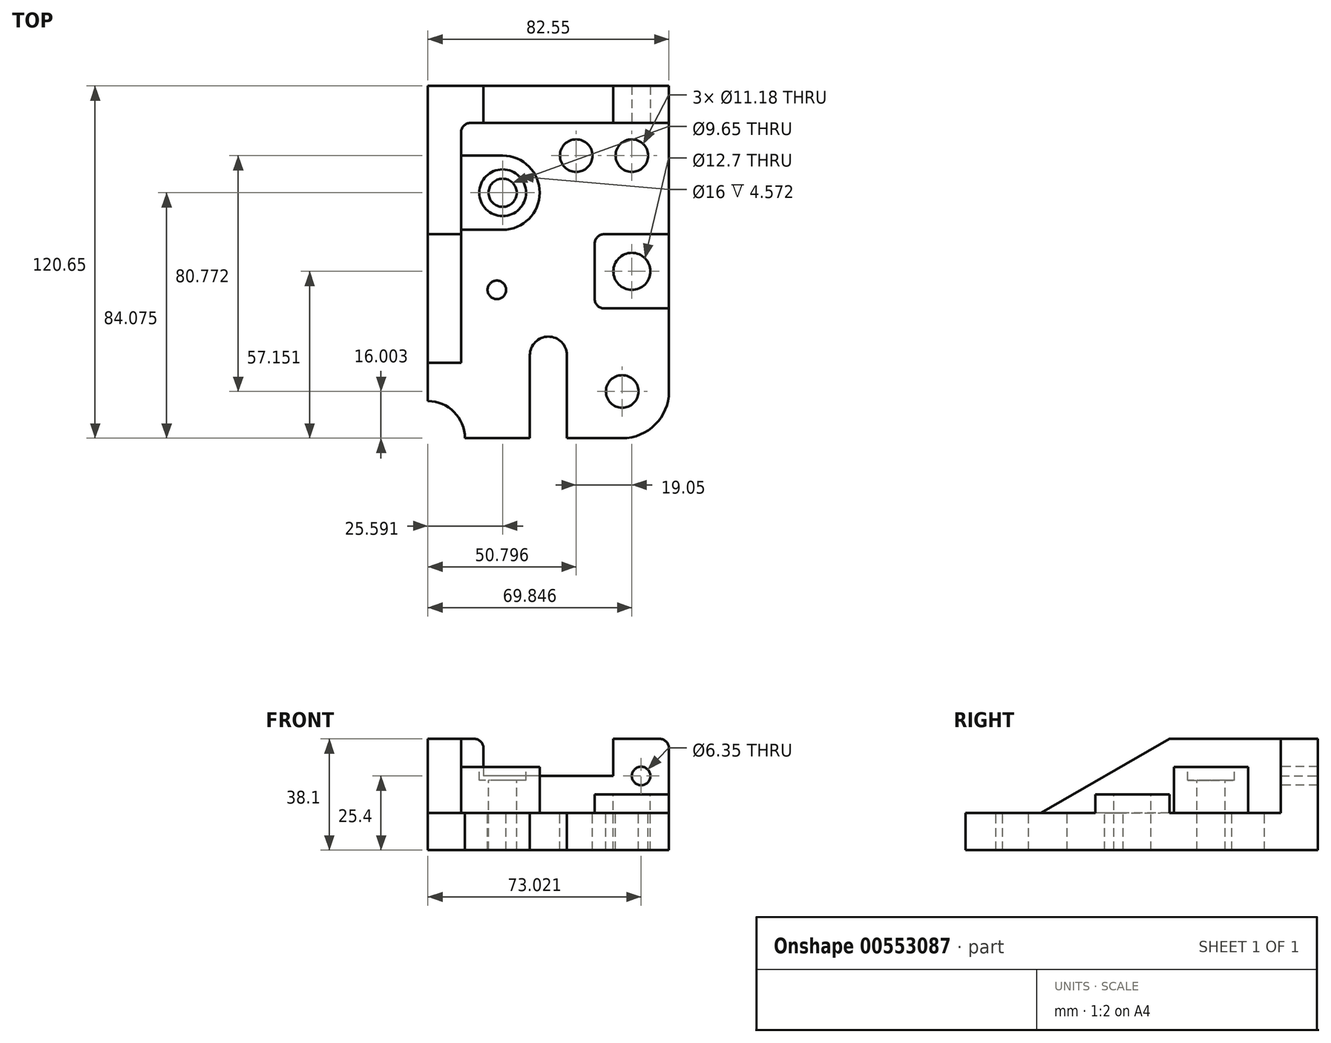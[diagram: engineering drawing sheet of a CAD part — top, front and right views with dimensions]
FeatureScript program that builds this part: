
annotation { "Feature Type Name" : "Feature", "Feature Type Description" : "" }
export const myFeature = defineFeature(function(context is Context, id is Id, definition is map)
    precondition{}
    {
        {
            var Q0;
            Q0=qCreatedBy(makeId("Top.planeOp"),FACE);
            var sketch = newSketch(context, id + "F0", { "sketchPlane" : qUnion([Q0])});
            skLineSegment(sketch, "E0.bottom", {"start": v(-42.14, 89.34) * mm, "end": v(40.4, 89.34) * mm});
            skLineSegment(sketch, "E0.top", {"start": v(-42.14, -31.3) * mm, "end": v(40.4, -31.3) * mm});
            skLineSegment(sketch, "E0.left", {"start": v(-42.14, 89.34) * mm, "end": v(-42.14, -31.3) * mm});
            skLineSegment(sketch, "E0.right", {"start": v(40.4, 89.34) * mm, "end": v(40.4, -31.3) * mm});
            skSolve(sketch);
        }
        {
            var Q0;
            Q0=makeQuery(id+"F0.imprint","IMPRINT",FACE,{"disambiguationData":[TD([[makeQuery(id+"F0.imprint","IMPRINT",EDGE,{"derivedFrom":sQuery(id+"F0.wireOp",EDGE,"E0.bottom")}),-1.0]])]});
            extrude(context, id + "F1", {"entities" : qUnion([Q0]), "depth" : 12.7 * mm, "offsetDistance" : 25.4 * mm});
        }
        {
            var Q0;
            Q0=makeQuery(id+"F1.opExtrude","CAP_FACE",FACE,{"disambiguationData":[OSD([sQuery(id+"F0.wireOp",EDGE,"E0.bottom"),sQuery(id+"F0.wireOp",EDGE,"E0.top"),sQuery(id+"F0.wireOp",EDGE,"E0.left"),sQuery(id+"F0.wireOp",EDGE,"E0.right")])],"isStart":false});
            var sketch = newSketch(context, id + "F2", { "sketchPlane" : qUnion([Q0])});
            skLineSegment(sketch, "E1.bottom", {"start": v(-42.14, 89.34) * mm, "end": v(40.4, 89.34) * mm});
            skLineSegment(sketch, "E1.top", {"start": v(-30.77, 76.64) * mm, "end": v(40.4, 76.64) * mm});
            skLineSegment(sketch, "E1.left", {"start": v(-42.14, 89.34) * mm, "end": v(-42.14, 76.64) * mm});
            skLineSegment(sketch, "E1.right", {"start": v(40.4, 89.34) * mm, "end": v(40.4, 76.64) * mm});
            skLineSegment(sketch, "E2.bottom", {"start": v(-42.14, 89.34) * mm, "end": v(-30.77, 89.34) * mm});
            skLineSegment(sketch, "E2.top", {"start": v(-42.14, 38.54) * mm, "end": v(-30.77, 38.54) * mm});
            skLineSegment(sketch, "E2.left", {"start": v(-42.14, 89.34) * mm, "end": v(-42.14, 38.54) * mm});
            skLineSegment(sketch, "E2.right", {"start": v(-30.77, 76.64) * mm, "end": v(-30.77, 38.54) * mm});
            skSolve(sketch);
        }
        {
            var Q0;
            Q0=makeQuery(id+"F2.imprint","IMPRINT",FACE,{"disambiguationData":[TD([[makeQuery(id+"F2.imprint","IMPRINT",EDGE,{"derivedFrom":sQuery(id+"F2.wireOp",EDGE,"E1.bottom")}),-1.0]])]});
            extrude(context, id + "F3", {"entities" : qUnion([Q0]), "operationType" : NewBodyOperationType.ADD, "depth" : 25.4 * mm, "offsetDistance" : 25.4 * mm});
        }
        {
            var Q0;
            Q0=makeQuery(id+"F3.opExtrude","SWEPT_FACE",FACE,{"disambiguationData":[OSD([sQuery(id+"F2.wireOp",EDGE,"E2.right")])]});
            var sketch = newSketch(context, id + "F4", { "sketchPlane" : qUnion([Q0])});
            skLineSegment(sketch, "E3", {"start": v(38.54, 38.1) * mm, "end": v(-3.5, 38.1) * mm});
            skLineSegment(sketch, "E4", {"start": v(38.54, 38.1) * mm, "end": v(-5.45, 12.7) * mm});
            skLineSegment(sketch, "E5", {"start": v(38.54, 12.7) * mm, "end": v(-5.45, 12.7) * mm});
            skLineSegment(sketch, "E6", {"start": v(38.54, 38.1) * mm, "end": v(38.54, 12.7) * mm});
            skSolve(sketch);
        }
        {
            var Q0;
            Q0=makeQuery(id+"F4.imprint","IMPRINT",FACE,{"disambiguationData":[TD([[makeQuery(id+"F4.imprint","IMPRINT",EDGE,{"derivedFrom":sQuery(id+"F4.wireOp",EDGE,"E4")}),1.0]])]});
            var Q1;
            Q1=makeQuery(id+"F3.boolean.opBoolean","MERGE",FACE,{"derivedFrom":[makeQuery(id+"F1.opExtrude","SWEPT_FACE",FACE,{"disambiguationData":[OSD([sQuery(id+"F0.wireOp",EDGE,"E0.left")])]}),makeQuery(id+"F3.opExtrude","SWEPT_FACE",FACE,{"disambiguationData":[OSD([sQuery(id+"F2.wireOp",EDGE,"E2.left")])]})]});
            extrude(context, id + "F5", {"entities" : qUnion([Q0]), "operationType" : NewBodyOperationType.ADD, "endBound" : BoundingType.UP_TO_SURFACE, "oppositeDirection" : true, "depth" : 18.54 * mm, "endBoundEntityFace" : qUnion([Q1]), "offsetDistance" : 25.4 * mm});
        }
        {
            var Q0;
            Q0=makeQuery(id+"F3.boolean.opBoolean","MERGE",FACE,{"derivedFrom":[makeQuery(id+"F1.opExtrude","SWEPT_FACE",FACE,{"disambiguationData":[OSD([sQuery(id+"F0.wireOp",EDGE,"E0.bottom")])]}),makeQuery(id+"F3.opExtrude","SWEPT_FACE",FACE,{"disambiguationData":[OSD([sQuery(id+"F2.wireOp",EDGE,"E1.bottom"),sQuery(id+"F2.wireOp",EDGE,"E2.bottom")])]})]});
            var sketch = newSketch(context, id + "F6", { "sketchPlane" : qUnion([Q0])});
            skLineSegment(sketch, "E7.bottom", {"start": v(-21.36, 38.1) * mm, "end": v(23.1, 38.1) * mm});
            skLineSegment(sketch, "E7.top", {"start": v(-21.36, 25.4) * mm, "end": v(23.1, 25.4) * mm});
            skLineSegment(sketch, "E7.left", {"start": v(-21.36, 38.1) * mm, "end": v(-21.36, 25.4) * mm});
            skLineSegment(sketch, "E7.right", {"start": v(23.1, 38.1) * mm, "end": v(23.1, 25.4) * mm});
            skSolve(sketch);
        }
        {
            var Q0;
            Q0=makeQuery(id+"F6.imprint","IMPRINT",FACE,{"disambiguationData":[TD([[makeQuery(id+"F6.imprint","IMPRINT",EDGE,{"derivedFrom":sQuery(id+"F6.wireOp",EDGE,"E7.bottom")}),1.0]])]});
            extrude(context, id + "F7", {"entities" : qUnion([Q0]), "operationType" : NewBodyOperationType.REMOVE, "oppositeDirection" : true, "depth" : 25.4 * mm, "offsetDistance" : 25.4 * mm});
        }
        {
            var Q0;
            Q0=makeQuery(id+"F1.opExtrude","CAP_FACE",FACE,{"disambiguationData":[OSD([sQuery(id+"F0.wireOp",EDGE,"E0.bottom"),sQuery(id+"F0.wireOp",EDGE,"E0.top"),sQuery(id+"F0.wireOp",EDGE,"E0.left"),sQuery(id+"F0.wireOp",EDGE,"E0.right")])],"isStart":false});
            var sketch = newSketch(context, id + "F8", { "sketchPlane" : qUnion([Q0])});
            skLineSegment(sketch, "E8.bottom", {"start": v(40.4, 13.14) * mm, "end": v(15, 13.14) * mm});
            skLineSegment(sketch, "E8.top", {"start": v(40.4, 38.54) * mm, "end": v(15, 38.54) * mm});
            skLineSegment(sketch, "E8.left", {"start": v(40.4, 13.14) * mm, "end": v(40.4, 38.54) * mm});
            skLineSegment(sketch, "E8.right", {"start": v(15, 13.14) * mm, "end": v(15, 38.54) * mm});
            skSolve(sketch);
        }
        {
            var Q0;
            Q0=makeQuery(id+"F8.imprint","IMPRINT",FACE,{"disambiguationData":[TD([[makeQuery(id+"F8.imprint","IMPRINT",EDGE,{"derivedFrom":sQuery(id+"F8.wireOp",EDGE,"E8.bottom")}),-1.0]])]});
            extrude(context, id + "F9", {"entities" : qUnion([Q0]), "operationType" : NewBodyOperationType.ADD, "depth" : 6.35 * mm, "offsetDistance" : 25.4 * mm});
        }
        {
            var Q0;
            Q0=makeQuery(id+"F9.opExtrude","CAP_FACE",FACE,{"disambiguationData":[OSD([sQuery(id+"F8.wireOp",EDGE,"E8.bottom"),sQuery(id+"F8.wireOp",EDGE,"E8.top"),sQuery(id+"F8.wireOp",EDGE,"E8.left"),sQuery(id+"F8.wireOp",EDGE,"E8.right")])],"isStart":false});
            var sketch = newSketch(context, id + "F10", { "sketchPlane" : qUnion([Q0])});
            skCircle(sketch, "E9", {"center": v(27.7, 25.84) * mm, "radius": 6.35 * mm});
            skPoint(sketch, "E9.centerSnap0", {"position": v(27.7, 13.14) * mm});
            skPoint(sketch, "E9.centerSnap1", {"position": v(40.4, 25.84) * mm});
            skSolve(sketch);
        }
        {
            var Q0;
            Q0=makeQuery(id+"F10.imprint","IMPRINT",FACE,{"disambiguationData":[TD([[makeQuery(id+"F10.imprint","IMPRINT",EDGE,{"derivedFrom":sQuery(id+"F10.wireOp",EDGE,"E9")}),1.0]])]});
            extrude(context, id + "F11", {"entities" : qUnion([Q0]), "operationType" : NewBodyOperationType.REMOVE, "endBound" : BoundingType.THROUGH_ALL, "oppositeDirection" : true, "depth" : 25.4 * mm, "offsetDistance" : 25.4 * mm});
        }
        {
            var Q0;
            Q0=makeQuery(id+"F1.opExtrude","CAP_FACE",FACE,{"disambiguationData":[OSD([sQuery(id+"F0.wireOp",EDGE,"E0.bottom"),sQuery(id+"F0.wireOp",EDGE,"E0.top"),sQuery(id+"F0.wireOp",EDGE,"E0.left"),sQuery(id+"F0.wireOp",EDGE,"E0.right")])],"isStart":false});
            var sketch = newSketch(context, id + "F12", { "sketchPlane" : qUnion([Q0])});
            skLineSegment(sketch, "E10.bottom", {"start": v(-30.77, 40.07) * mm, "end": v(-16.55, 40.07) * mm});
            skLineSegment(sketch, "E10.top", {"start": v(-30.77, 65.47) * mm, "end": v(-16.55, 65.47) * mm});
            skLineSegment(sketch, "E10.left", {"start": v(-30.77, 40.07) * mm, "end": v(-30.77, 65.47) * mm});
            skArc(sketch, "E11", {"start": v(-16.55, 40.07) * mm, "mid": v(-3.85, 52.77) * mm, "end": v(-16.55, 65.47) * mm});
            skSolve(sketch);
        }
        {
            var Q0;
            Q0=makeQuery(id+"F12.imprint","IMPRINT",FACE,{"disambiguationData":[TD([[makeQuery(id+"F12.imprint","IMPRINT",EDGE,{"derivedFrom":sQuery(id+"F12.wireOp",EDGE,"E10.bottom")}),1.0]])]});
            extrude(context, id + "F13", {"entities" : qUnion([Q0]), "operationType" : NewBodyOperationType.ADD, "depth" : 15.75 * mm, "offsetDistance" : 25.4 * mm});
        }
        {
            var Q0;
            Q0=makeQuery(id+"F13.opExtrude","CAP_FACE",FACE,{"disambiguationData":[OSD([sQuery(id+"F12.wireOp",EDGE,"E10.bottom"),sQuery(id+"F12.wireOp",EDGE,"E10.top"),sQuery(id+"F12.wireOp",EDGE,"E10.left"),sQuery(id+"F12.wireOp",EDGE,"E11")])],"isStart":false});
            var sketch = newSketch(context, id + "F14", { "sketchPlane" : qUnion([Q0])});
            skCircle(sketch, "E12", {"center": v(-16.55, 52.77) * mm, "radius": 4.83 * mm});
            skSolve(sketch);
        }
        {
            var Q0;
            Q0=makeQuery(id+"F14.imprint","IMPRINT",FACE,{"disambiguationData":[TD([[makeQuery(id+"F14.imprint","IMPRINT",EDGE,{"derivedFrom":sQuery(id+"F14.wireOp",EDGE,"E12")}),1.0]])]});
            extrude(context, id + "F15", {"entities" : qUnion([Q0]), "operationType" : NewBodyOperationType.REMOVE, "endBound" : BoundingType.THROUGH_ALL, "oppositeDirection" : true, "depth" : 25.4 * mm, "offsetDistance" : 25.4 * mm});
        }
        {
            var Q0;
            Q0=makeQuery(id+"F13.opExtrude","CAP_FACE",FACE,{"disambiguationData":[OSD([sQuery(id+"F12.wireOp",EDGE,"E10.bottom"),sQuery(id+"F12.wireOp",EDGE,"E10.top"),sQuery(id+"F12.wireOp",EDGE,"E10.left"),sQuery(id+"F12.wireOp",EDGE,"E11")])],"isStart":false});
            var sketch = newSketch(context, id + "F16", { "sketchPlane" : qUnion([Q0])});
            skCircle(sketch, "E13", {"center": v(-16.55, 52.77) * mm, "radius": 8 * mm});
            skSolve(sketch);
        }
        {
            var Q0;
            Q0=makeQuery(id+"F16.imprint","IMPRINT",FACE,{"disambiguationData":[TD([[makeQuery(id+"F16.imprint","IMPRINT",EDGE,{"derivedFrom":sQuery(id+"F16.wireOp",EDGE,"E13")}),1.0]])]});
            extrude(context, id + "F17", {"entities" : qUnion([Q0]), "operationType" : NewBodyOperationType.REMOVE, "oppositeDirection" : true, "depth" : 4.57 * mm, "offsetDistance" : 25.4 * mm});
        }
        {
            var Q0;
            Q0=makeQuery(id+"F1.opExtrude","CAP_FACE",FACE,{"disambiguationData":[OSD([sQuery(id+"F0.wireOp",EDGE,"E0.bottom"),sQuery(id+"F0.wireOp",EDGE,"E0.top"),sQuery(id+"F0.wireOp",EDGE,"E0.left"),sQuery(id+"F0.wireOp",EDGE,"E0.right")])],"isStart":false});
            var sketch = newSketch(context, id + "F18", { "sketchPlane" : qUnion([Q0])});
            skLineSegment(sketch, "E14", {"start": v(-0.87, -31.3) * mm, "end": v(-0.87, 76.64) * mm, "construction": true});
            skLineSegment(sketch, "E15.bottom", {"start": v(-7.22, -31.3) * mm, "end": v(5.48, -31.3) * mm});
            skLineSegment(sketch, "E15.top", {"start": v(-7.22, -2.86) * mm, "end": v(5.48, -2.86) * mm});
            skLineSegment(sketch, "E15.left", {"start": v(-7.22, -31.3) * mm, "end": v(-7.22, -2.86) * mm});
            skLineSegment(sketch, "E15.right", {"start": v(5.48, -31.3) * mm, "end": v(5.48, -2.86) * mm});
            skArc(sketch, "E16", {"start": v(5.48, -2.86) * mm, "mid": v(-0.87, 3.49) * mm, "end": v(-7.22, -2.86) * mm});
            skSolve(sketch);
        }
        {
            var Q0;
            Q0=makeQuery(id+"F18.imprint","IMPRINT",FACE,{"disambiguationData":[TD([[makeQuery(id+"F18.imprint","IMPRINT",EDGE,{"derivedFrom":sQuery(id+"F18.wireOp",EDGE,"E15.bottom")}),1.0]])]});
            var Q1;
            Q1=makeQuery(id+"F18.imprint","IMPRINT",FACE,{"disambiguationData":[TD([[makeQuery(id+"F18.imprint","IMPRINT",EDGE,{"derivedFrom":sQuery(id+"F18.wireOp",EDGE,"E15.top")}),1.0]])]});
            extrude(context, id + "F19", {"entities" : qUnion([Q0, Q1]), "operationType" : NewBodyOperationType.REMOVE, "oppositeDirection" : true, "depth" : 25.4 * mm, "offsetDistance" : 25.4 * mm});
        }
        {
            var Q0;
            Q0=makeQuery(id+"F1.opExtrude","CAP_FACE",FACE,{"disambiguationData":[OSD([sQuery(id+"F0.wireOp",EDGE,"E0.bottom"),sQuery(id+"F0.wireOp",EDGE,"E0.top"),sQuery(id+"F0.wireOp",EDGE,"E0.left"),sQuery(id+"F0.wireOp",EDGE,"E0.right")])],"isStart":false});
            var sketch = newSketch(context, id + "F20", { "sketchPlane" : qUnion([Q0])});
            skCircle(sketch, "E17", {"center": v(-18.52, 19.5) * mm, "radius": 3.17 * mm});
            skCircle(sketch, "E18", {"center": v(24.4, -15.3) * mm, "radius": 5.59 * mm});
            skCircle(sketch, "E19", {"center": v(27.7, 65.47) * mm, "radius": 5.59 * mm});
            skCircle(sketch, "E20", {"center": v(8.66, 65.47) * mm, "radius": 5.59 * mm});
            skSolve(sketch);
        }
        {
            var Q0;
            Q0=makeQuery(id+"F20.imprint","IMPRINT",FACE,{"disambiguationData":[TD([[makeQuery(id+"F20.imprint","IMPRINT",EDGE,{"derivedFrom":sQuery(id+"F20.wireOp",EDGE,"E17")}),1.0]])]});
            var Q1;
            Q1=makeQuery(id+"F20.imprint","IMPRINT",FACE,{"disambiguationData":[TD([[makeQuery(id+"F20.imprint","IMPRINT",EDGE,{"derivedFrom":sQuery(id+"F20.wireOp",EDGE,"E18")}),1.0]])]});
            var Q2;
            Q2=makeQuery(id+"F20.imprint","IMPRINT",FACE,{"disambiguationData":[TD([[makeQuery(id+"F20.imprint","IMPRINT",EDGE,{"derivedFrom":sQuery(id+"F20.wireOp",EDGE,"E19")}),1.0]])]});
            var Q3;
            Q3=makeQuery(id+"F20.imprint","IMPRINT",FACE,{"disambiguationData":[TD([[makeQuery(id+"F20.imprint","IMPRINT",EDGE,{"derivedFrom":sQuery(id+"F20.wireOp",EDGE,"E20")}),1.0]])]});
            extrude(context, id + "F21", {"entities" : qUnion([Q0, Q1, Q2, Q3]), "operationType" : NewBodyOperationType.REMOVE, "endBound" : BoundingType.THROUGH_ALL, "oppositeDirection" : true, "depth" : 25.4 * mm, "offsetDistance" : 25.4 * mm});
        }
        {
            var Q0;
            Q0=makeQuery(id+"F3.opExtrude","SWEPT_FACE",FACE,{"disambiguationData":[OSD([sQuery(id+"F2.wireOp",EDGE,"E1.top")])]});
            var sketch = newSketch(context, id + "F22", { "sketchPlane" : qUnion([Q0])});
            skCircle(sketch, "E21", {"center": v(30.88, 25.4) * mm, "radius": 3.18 * mm});
            skPoint(sketch, "E21.centerSnap0", {"position": v(30.88, 38.1) * mm});
            skSolve(sketch);
        }
        {
            var Q0;
            Q0=makeQuery(id+"F22.imprint","IMPRINT",FACE,{"disambiguationData":[TD([[makeQuery(id+"F22.imprint","IMPRINT",EDGE,{"derivedFrom":sQuery(id+"F22.wireOp",EDGE,"E21")}),1.0]])]});
            extrude(context, id + "F23", {"entities" : qUnion([Q0]), "operationType" : NewBodyOperationType.REMOVE, "oppositeDirection" : true, "depth" : 25.4 * mm, "offsetDistance" : 25.4 * mm});
        }
        {
            var Q0;
            Q0=makeQuery(id+"F1.opExtrude","CAP_FACE",FACE,{"disambiguationData":[OSD([sQuery(id+"F0.wireOp",EDGE,"E0.bottom"),sQuery(id+"F0.wireOp",EDGE,"E0.top"),sQuery(id+"F0.wireOp",EDGE,"E0.left"),sQuery(id+"F0.wireOp",EDGE,"E0.right")])],"isStart":false});
            var sketch = newSketch(context, id + "F24", { "sketchPlane" : qUnion([Q0])});
            skCircle(sketch, "E22", {"center": v(-42.14, -31.3) * mm, "radius": 12.7 * mm});
            skSolve(sketch);
        }
        {
            var Q0;
            {var subQ0=sQuery(id+"F24.wireOp",EDGE,"E22");var subQ1=sQuery(id+"F0.wireOp",EDGE,"E0.left");var subQ2=makeQuery(id+"F1.opExtrude","CAP_EDGE",EDGE,{"disambiguationData":[OSD([subQ1])],"isStart":false});var subQ3=makeQuery(id+"F24.imprint","INTERSECT",VERTEX,{"derivedFrom":[subQ2,subQ0]});Q0=makeQuery(id+"F24.imprint","IMPRINT",FACE,{"disambiguationData":[TD([[makeQuery(id+"F24.imprint","IMPRINT",EDGE,{"disambiguationData":[TD([[subQ3,1.0]])],"derivedFrom":subQ0}),1.0]])]});}
            extrude(context, id + "F25", {"entities" : qUnion([Q0]), "operationType" : NewBodyOperationType.REMOVE, "oppositeDirection" : true, "depth" : 25.4 * mm, "offsetDistance" : 25.4 * mm});
        }
        {
            var Q0;
            Q0=makeQuery(id+"F1.opExtrude","SWEPT_EDGE",EDGE,{"disambiguationData":[OSD([sQuery(id+"F0.wireOp",EDGE,"E0.top"),sQuery(id+"F0.wireOp",EDGE,"E0.right")])]});
            fillet(context, id + "F26", {"entities" : qUnion([Q0]), "radius" : 16 * mm, "tangentPropagation" : true, "allowEdgeOverflow" : false});
        }
        {
            var Q0;
            {var subQ0=sQuery(id+"F4.wireOp",EDGE,"E5");var subQ1=sQuery(id+"F4.wireOp",EDGE,"E4");var subQ2=sQuery(id+"F2.wireOp",EDGE,"E2.right");Q0=makeQuery(id+"F13.boolean.opBoolean","SPLIT",EDGE,{"disambiguationData":[TD([makeQuery(id+"F5.opExtrude","SWEPT_FACE",FACE,{"disambiguationData":[OSD([subQ1])]})])],"derivedFrom":makeQuery(id+"F5.boolean.opBoolean","MERGE",EDGE,{"derivedFrom":[makeQuery(id+"F3.opExtrude","CAP_EDGE",EDGE,{"disambiguationData":[OSD([subQ2])],"isStart":true}),makeQuery(id+"F5.opExtrude","CAP_EDGE",EDGE,{"disambiguationData":[OSD([subQ0])],"isStart":true})]})});}
            var Q1;
            Q1=makeQuery(id+"F13.opExtrude","SWEPT_EDGE",EDGE,{"disambiguationData":[OSD([sQuery(id+"F2.wireOp",EDGE,"E2.right"),sQuery(id+"F4.wireOp",EDGE,"E5"),sQuery(id+"F12.wireOp",EDGE,"E10.bottom"),sQuery(id+"F12.wireOp",EDGE,"E10.left")])]});
            var Q2;
            Q2=makeQuery(id+"F13.opExtrude","CAP_EDGE",EDGE,{"disambiguationData":[OSD([sQuery(id+"F12.wireOp",EDGE,"E10.bottom")])],"isStart":true});
            var Q3;
            Q3=makeQuery(id+"F13.opExtrude","CAP_EDGE",EDGE,{"disambiguationData":[OSD([sQuery(id+"F12.wireOp",EDGE,"E10.left")])],"isStart":false});
            var Q4;
            Q4=makeQuery(id+"F3.opExtrude","CAP_EDGE",EDGE,{"disambiguationData":[OSD([sQuery(id+"F2.wireOp",EDGE,"E1.top")])],"isStart":true});
            var Q5;
            Q5=makeQuery(id+"F13.opExtrude","SWEPT_EDGE",EDGE,{"disambiguationData":[OSD([sQuery(id+"F2.wireOp",EDGE,"E2.right"),sQuery(id+"F4.wireOp",EDGE,"E5"),sQuery(id+"F12.wireOp",EDGE,"E10.top"),sQuery(id+"F12.wireOp",EDGE,"E10.left")])]});
            var Q6;
            Q6=makeQuery(id+"F3.opExtrude","SWEPT_EDGE",EDGE,{"disambiguationData":[OSD([sQuery(id+"F2.wireOp",EDGE,"E1.top"),sQuery(id+"F2.wireOp",EDGE,"E2.right")])]});
            var Q7;
            Q7=makeQuery(id+"F9.opExtrude","SWEPT_EDGE",EDGE,{"disambiguationData":[OSD([sQuery(id+"F8.wireOp",EDGE,"E8.bottom"),sQuery(id+"F8.wireOp",EDGE,"E8.right")])]});
            var Q8;
            Q8=makeQuery(id+"F9.opExtrude","SWEPT_EDGE",EDGE,{"disambiguationData":[OSD([sQuery(id+"F8.wireOp",EDGE,"E8.top"),sQuery(id+"F8.wireOp",EDGE,"E8.right")])]});
            var Q9;
            Q9=makeQuery(id+"F7.boolean.opBoolean","COPY",EDGE,{"derivedFrom":makeQuery(id+"F7.opExtrude","SWEPT_EDGE",EDGE,{"disambiguationData":[OSD([sQuery(id+"F2.wireOp",EDGE,"E1.bottom"),sQuery(id+"F2.wireOp",EDGE,"E2.bottom"),sQuery(id+"F6.wireOp",EDGE,"E7.bottom"),sQuery(id+"F6.wireOp",EDGE,"E7.right")])]})});
            var Q10;
            Q10=makeQuery(id+"F3.opExtrude","CAP_EDGE",EDGE,{"disambiguationData":[OSD([sQuery(id+"F2.wireOp",EDGE,"E1.right")])],"isStart":false});
            var Q11;
            Q11=makeQuery(id+"F7.boolean.opBoolean","COPY",EDGE,{"derivedFrom":makeQuery(id+"F7.opExtrude","SWEPT_EDGE",EDGE,{"disambiguationData":[OSD([sQuery(id+"F2.wireOp",EDGE,"E1.bottom"),sQuery(id+"F2.wireOp",EDGE,"E2.bottom"),sQuery(id+"F6.wireOp",EDGE,"E7.bottom"),sQuery(id+"F6.wireOp",EDGE,"E7.left")])]})});
            var Q12;
            Q12=makeQuery(id+"F9.opExtrude","CAP_EDGE",EDGE,{"disambiguationData":[OSD([sQuery(id+"F8.wireOp",EDGE,"E8.bottom")])],"isStart":true});
            fillet(context, id + "F27", {"entities" : qUnion([Q0, Q1, Q2, Q3, Q4, Q5, Q6, Q7, Q8, Q9, Q10, Q11, Q12]), "radius" : 3.17 * mm, "tangentPropagation" : true, "allowEdgeOverflow" : false});
        }
    });
